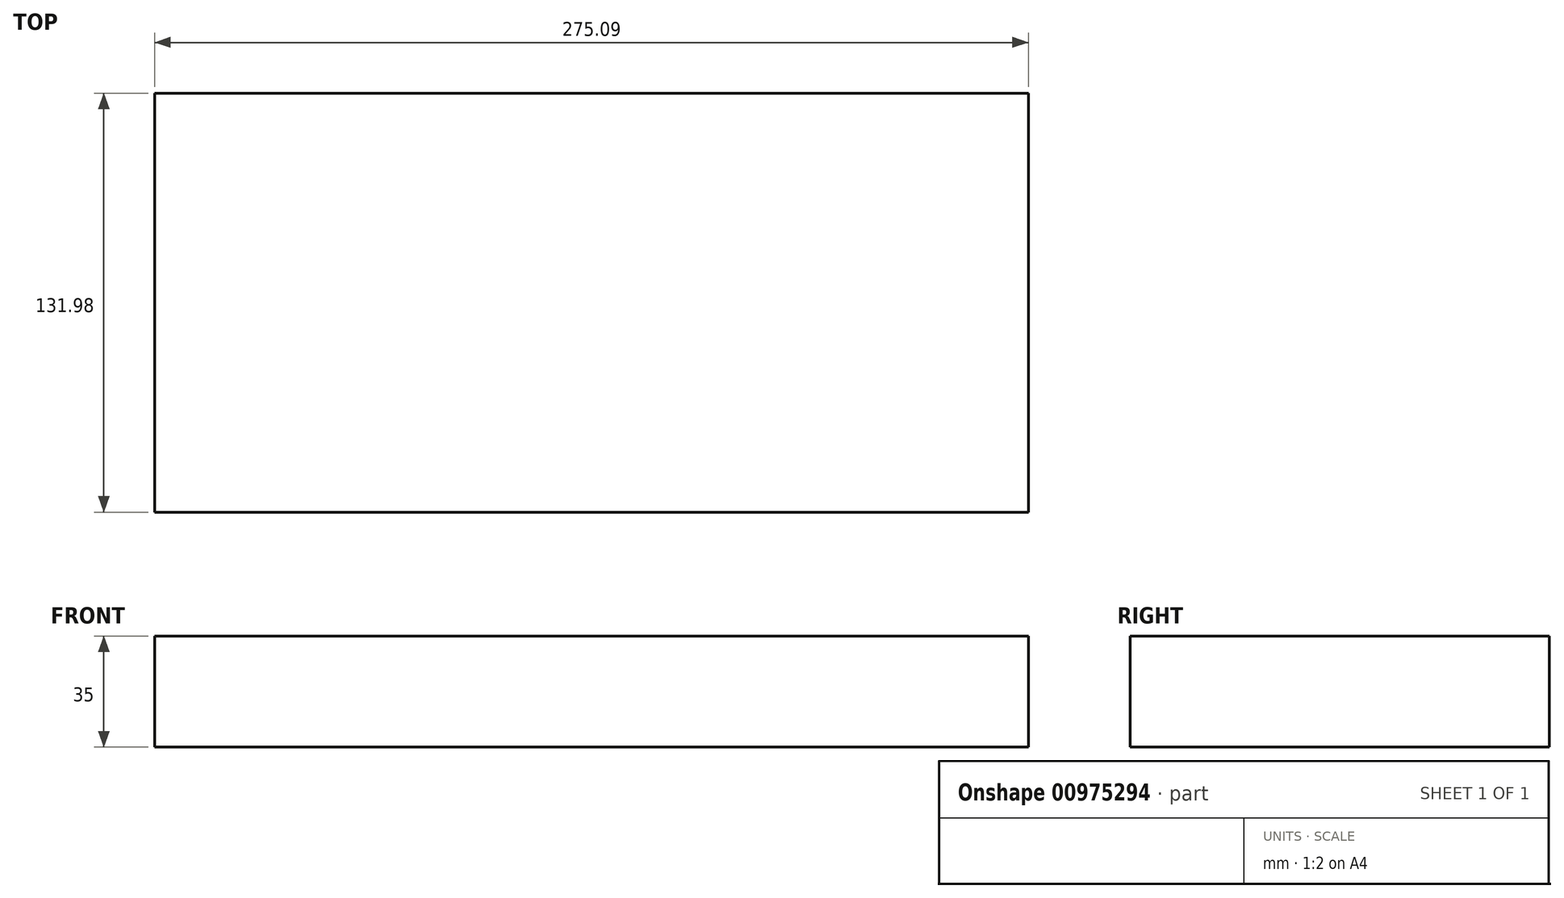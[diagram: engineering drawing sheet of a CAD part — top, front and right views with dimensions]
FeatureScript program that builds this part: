
annotation { "Feature Type Name" : "Feature", "Feature Type Description" : "" }
export const myFeature = defineFeature(function(context is Context, id is Id, definition is map)
    precondition{}
    {
        {
            var Q0;
            Q0=qCreatedBy(makeId("Top.planeOp"),FACE);
            var sketch = newSketch(context, id + "F0", { "sketchPlane" : qUnion([Q0])});
            skLineSegment(sketch, "E0.bottom", {"start": v(-131.53, 63.29) * mm, "end": v(143.56, 63.29) * mm});
            skLineSegment(sketch, "E0.top", {"start": v(-131.53, -68.69) * mm, "end": v(143.56, -68.69) * mm});
            skLineSegment(sketch, "E0.left", {"start": v(-131.53, 63.29) * mm, "end": v(-131.53, -68.69) * mm});
            skLineSegment(sketch, "E0.right", {"start": v(143.56, 63.29) * mm, "end": v(143.56, -68.69) * mm});
            skSolve(sketch);
        }
        {
            var Q0;
            Q0=makeQuery(id+"F0.imprint","IMPRINT",FACE,{"disambiguationData":[TD([[makeQuery(id+"F0.imprint","IMPRINT",EDGE,{"derivedFrom":sQuery(id+"F0.wireOp",EDGE,"E0.bottom")}),-1.0]])]});
            extrude(context, id + "F1", {"entities" : qUnion([Q0]), "depth" : 35 * mm, "offsetDistance" : 25.4 * mm});
        }
    });
